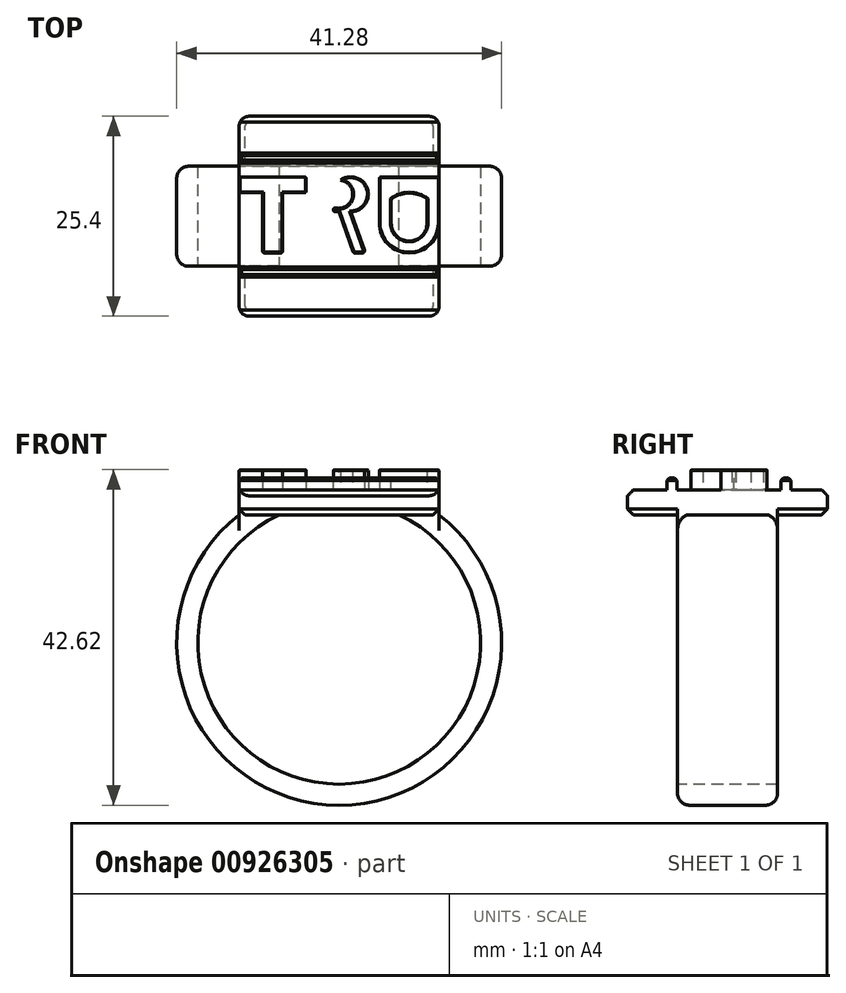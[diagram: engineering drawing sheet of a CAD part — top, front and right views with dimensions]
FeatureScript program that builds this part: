
annotation { "Feature Type Name" : "Feature", "Feature Type Description" : "" }
export const myFeature = defineFeature(function(context is Context, id is Id, definition is map)
    precondition{}
    {
        {
            var Q0;
            Q0=qCreatedBy(makeId("Top.planeOp"),FACE);
            var sketch = newSketch(context, id + "F0", { "sketchPlane" : qUnion([Q0])});
            skLineSegment(sketch, "E0.bottom", {"start": v(12.7, -12.7) * mm, "end": v(-12.7, -12.7) * mm});
            skLineSegment(sketch, "E0.top", {"start": v(12.7, 12.7) * mm, "end": v(-12.7, 12.7) * mm});
            skLineSegment(sketch, "E0.left", {"start": v(12.7, -12.7) * mm, "end": v(12.7, 12.7) * mm});
            skLineSegment(sketch, "E0.right", {"start": v(-12.7, -12.7) * mm, "end": v(-12.7, 12.7) * mm});
            skPoint(sketch, "E0.middle", {"position": v(0, 0) * mm});
            skSolve(sketch);
        }
        {
            var Q0;
            Q0=makeQuery(id+"F0.imprint","IMPRINT",FACE,{"disambiguationData":[TD([[makeQuery(id+"F0.imprint","IMPRINT",EDGE,{"derivedFrom":sQuery(id+"F0.wireOp",EDGE,"E0.bottom")}),-1.0]])]});
            extrude(context, id + "F1", {"entities" : qUnion([Q0]), "depth" : 3.17 * mm, "offsetDistance" : 25.4 * mm});
        }
        {
            var Q0;
            Q0=qCreatedBy(makeId("Front.planeOp"),FACE);
            var sketch = newSketch(context, id + "F2", { "sketchPlane" : qUnion([Q0])});
            skArc(sketch, "E1", {"start": v(-10.16, 0) * mm, "mid": v(0, -35.44) * mm, "end": v(10.16, 0) * mm});
            skSolve(sketch);
        }
        {
            var Q0;
            Q0=makeQuery(id+"F1.opExtrude","CAP_FACE",FACE,{"disambiguationData":[OSD([sQuery(id+"F0.wireOp",EDGE,"E0.bottom"),sQuery(id+"F0.wireOp",EDGE,"E0.top"),sQuery(id+"F0.wireOp",EDGE,"E0.left"),sQuery(id+"F0.wireOp",EDGE,"E0.right")])],"isStart":true});
            var sketch = newSketch(context, id + "F3", { "sketchPlane" : qUnion([Q0])});
            skLineSegment(sketch, "E2.bottom", {"start": v(-7.62, -6.35) * mm, "end": v(-12.7, -6.35) * mm});
            skLineSegment(sketch, "E2.top", {"start": v(-7.62, 6.35) * mm, "end": v(-12.7, 6.35) * mm});
            skLineSegment(sketch, "E2.left", {"start": v(-7.62, -6.35) * mm, "end": v(-7.62, 6.35) * mm});
            skLineSegment(sketch, "E2.right", {"start": v(-12.7, -6.35) * mm, "end": v(-12.7, 6.35) * mm});
            skPoint(sketch, "E2.middle", {"position": v(-10.16, 0) * mm});
            skSolve(sketch);
        }
        {
            var Q0;
            Q0 = qSketchRegion(id + "F3", true);
            var Q1;
            Q1 = qConstructionFilter(qBodyType(qCreatedBy(id + "F3" ,EDGE), BodyType.WIRE), ConstructionObject.NO);
            var Q2;
            Q2 = qConstructionFilter(qBodyType(qCreatedBy(id + "F2" ,EDGE), BodyType.WIRE), ConstructionObject.NO);
            sweep(context, id + "F4", {"operationType" : NewBodyOperationType.ADD, "profiles" : qUnion([Q0]), "surfaceProfiles" : qUnion([Q1]), "path" : qUnion([Q2])});
        }
        {
            var Q0;
            Q0=makeQuery(id+"F1.opExtrude","CAP_FACE",FACE,{"disambiguationData":[OSD([sQuery(id+"F0.wireOp",EDGE,"E0.bottom"),sQuery(id+"F0.wireOp",EDGE,"E0.top"),sQuery(id+"F0.wireOp",EDGE,"E0.left"),sQuery(id+"F0.wireOp",EDGE,"E0.right")])],"isStart":false});
            var sketch = newSketch(context, id + "F5", { "sketchPlane" : qUnion([Q0])});
            skLineSegment(sketch, "E3.bottom", {"start": v(-9.71, 2.99) * mm, "end": v(-7.17, 2.99) * mm});
            skLineSegment(sketch, "E3.top", {"start": v(-9.71, -4.66) * mm, "end": v(-7.17, -4.66) * mm});
            skLineSegment(sketch, "E3.left", {"start": v(-9.71, 2.99) * mm, "end": v(-9.71, -4.66) * mm});
            skLineSegment(sketch, "E3.right", {"start": v(-7.17, 2.99) * mm, "end": v(-7.17, -4.66) * mm});
            skLineSegment(sketch, "E4.bottom", {"start": v(-12.7, 5) * mm, "end": v(-4.19, 5) * mm});
            skLineSegment(sketch, "E4.top", {"start": v(-12.7, 2.99) * mm, "end": v(-4.19, 2.99) * mm});
            skLineSegment(sketch, "E4.left", {"start": v(-12.7, 5) * mm, "end": v(-12.7, 2.99) * mm});
            skLineSegment(sketch, "E4.right", {"start": v(-4.19, 5) * mm, "end": v(-4.19, 2.99) * mm});
            skLineSegment(sketch, "E5", {"start": v(-9.71, -4.66) * mm, "end": v(-12.7, -4.66) * mm});
            skLineSegment(sketch, "E6", {"start": v(-12.7, -4.66) * mm, "end": v(-9.71, -4.66) * mm});
            skLineSegment(sketch, "E7", {"start": v(12.7, -4.66) * mm, "end": v(-7.17, -4.66) * mm});
            skLineSegment(sketch, "E8.bottom", {"start": v(-0.74, 5) * mm, "end": v(-3.28, 5) * mm});
            skLineSegment(sketch, "E8.top", {"start": v(-0.74, -4.66) * mm, "end": v(-3.28, -4.66) * mm});
            skLineSegment(sketch, "E9", {"start": v(-0.74, 5) * mm, "end": v(1.48, 5) * mm});
            skLineSegment(sketch, "E10", {"start": v(5.1, 5) * mm, "end": v(5.1, -0.86) * mm});
            skLineSegment(sketch, "E11", {"start": v(12.7, 5) * mm, "end": v(12.7, -0.86) * mm});
            skLineSegment(sketch, "E12", {"start": v(-12.7, 5) * mm, "end": v(14.85, 5) * mm});
            skLineSegment(sketch, "E13", {"start": v(6.62, 5) * mm, "end": v(6.62, -0.86) * mm});
            skLineSegment(sketch, "E14", {"start": v(11.18, 5) * mm, "end": v(11.18, -0.86) * mm});
            skCircle(sketch, "E15", {"center": v(8.9, -0.86) * mm, "radius": 2.28 * mm});
            skLineSegment(sketch, "E16", {"start": v(6.62, -0.86) * mm, "end": v(5.1, -0.86) * mm});
            skLineSegment(sketch, "E17", {"start": v(11.18, -0.86) * mm, "end": v(12.7, -0.86) * mm});
            skCircle(sketch, "E18", {"center": v(8.9, -0.86) * mm, "radius": 3.8 * mm});
            skLineSegment(sketch, "E19", {"start": v(-3.28, 5) * mm, "end": v(-3.28, -4.66) * mm});
            skLineSegment(sketch, "E20", {"start": v(-0.74, -4.66) * mm, "end": v(-0.74, 5) * mm});
            skLineSegment(sketch, "E21", {"start": v(-0.74, 0.58) * mm, "end": v(1.48, 0.58) * mm});
            skCircle(sketch, "E22", {"center": v(1.48, 2.8) * mm, "radius": 2.22 * mm});
            skLineSegment(sketch, "E23", {"start": v(0, 0.58) * mm, "end": v(1.83, -4.66) * mm});
            skLineSegment(sketch, "E24", {"start": v(1.48, 0.58) * mm, "end": v(3.31, -4.66) * mm});
            skArc(sketch, "E25", {"start": v(-0.74, 1.14) * mm, "mid": v(1.73, 2.8) * mm, "end": v(-0.74, 4.45) * mm});
            skSolve(sketch);
        }
        {
            var Q0;
            {var subQ0=sQuery(id+"F5.wireOp",EDGE,"E4.left");Q0=makeQuery(id+"F5.imprint","IMPRINT",FACE,{"disambiguationData":[TD([[makeQuery(id+"F5.imprint","IMPRINT",EDGE,{"derivedFrom":subQ0}),-1.0]])]});}
            var Q1;
            Q1=makeQuery(id+"F5.imprint","IMPRINT",FACE,{"disambiguationData":[TD([[makeQuery(id+"F5.imprint","IMPRINT",EDGE,{"derivedFrom":sQuery(id+"F5.wireOp",EDGE,"E3.top")}),1.0]])]});
            var Q2;
            {var subQ1=sQuery(id+"F5.wireOp",EDGE,"E8.top");Q2=makeQuery(id+"F5.imprint","IMPRINT",FACE,{"disambiguationData":[TD([[makeQuery(id+"F5.imprint","IMPRINT",EDGE,{"derivedFrom":subQ1}),-1.0]])]});}
            var Q3;
            {var subQ4=sQuery(id+"F5.wireOp",EDGE,"E20");var subQ6=sQuery(id+"F5.wireOp",EDGE,"E12");var subQ7=makeQuery(id+"F5.imprint","INTERSECT",VERTEX,{"derivedFrom":[subQ6,subQ4]});Q3=makeQuery(id+"F5.imprint","IMPRINT",FACE,{"disambiguationData":[TD([[makeQuery(id+"F5.imprint","IMPRINT",EDGE,{"disambiguationData":[TD([[subQ7,-1.0]])],"derivedFrom":subQ6}),-1.0]])]});}
            var Q4;
            Q4=makeQuery(id+"F5.imprint","IMPRINT",FACE,{"disambiguationData":[TD([[makeQuery(id+"F5.imprint","IMPRINT",EDGE,{"derivedFrom":sQuery(id+"F5.wireOp",EDGE,"Z2IO4UIo-EBxe-1SLG-rrHU-Ieeh97X91HPy")}),-1.0]])]});
            var Q5;
            {var subQ0=sQuery(id+"F5.wireOp",EDGE,"E23");Q5=makeQuery(id+"F5.imprint","IMPRINT",FACE,{"disambiguationData":[TD([[makeQuery(id+"F5.imprint","IMPRINT",EDGE,{"derivedFrom":subQ0}),1.0]])]});}
            var Q6;
            {var subQ0=sQuery(id+"F5.wireOp",EDGE,"E10");Q6=makeQuery(id+"F5.imprint","IMPRINT",FACE,{"disambiguationData":[TD([[makeQuery(id+"F5.imprint","IMPRINT",EDGE,{"derivedFrom":subQ0}),1.0]])]});}
            var Q7;
            {var subQ0=sQuery(id+"F5.wireOp",EDGE,"E16");Q7=makeQuery(id+"F5.imprint","IMPRINT",FACE,{"disambiguationData":[TD([[makeQuery(id+"F5.imprint","IMPRINT",EDGE,{"derivedFrom":subQ0}),-1.0]])]});}
            var Q8;
            {var subQ1=sQuery(id+"F5.wireOp",EDGE,"E16");Q8=makeQuery(id+"F5.imprint","IMPRINT",FACE,{"disambiguationData":[TD([[makeQuery(id+"F5.imprint","IMPRINT",EDGE,{"derivedFrom":subQ1}),1.0]])]});}
            var Q9;
            {var subQ1=sQuery(id+"F5.wireOp",EDGE,"E11");Q9=makeQuery(id+"F5.imprint","IMPRINT",FACE,{"disambiguationData":[TD([[makeQuery(id+"F5.imprint","IMPRINT",EDGE,{"derivedFrom":subQ1}),1.0]])]});}
            var Q10;
            {var subQ1=sQuery(id+"F5.wireOp",EDGE,"E14");var subQ3=sQuery(id+"F5.wireOp",EDGE,"E18");var subQ4=makeQuery(id+"F5.imprint","INTERSECT",VERTEX,{"derivedFrom":[subQ1,subQ3]});Q10=makeQuery(id+"F5.imprint","IMPRINT",FACE,{"disambiguationData":[TD([[makeQuery(id+"F5.imprint","IMPRINT",EDGE,{"disambiguationData":[TD([[subQ4,1.0]])],"derivedFrom":subQ3}),1.0]])]});}
            var Q11;
            {var subQ0=sQuery(id+"F5.wireOp",EDGE,"E22");var subQ1=makeQuery(id+"F5.imprint","INTERSECT",VERTEX,{"derivedFrom":[sQuery(id+"F5.wireOp",EDGE,"E12"),subQ0]});Q11=makeQuery(id+"F5.imprint","IMPRINT",FACE,{"disambiguationData":[TD([[makeQuery(id+"F5.imprint","IMPRINT",EDGE,{"disambiguationData":[TD([[subQ1,-1.0]])],"derivedFrom":subQ0}),1.0]])]});}
            var Q12;
            {var subQ1=sQuery(id+"F5.wireOp",EDGE,"E21");var subQ6=sQuery(id+"F5.wireOp",EDGE,"E20");var subQ7=makeQuery(id+"F5.imprint","INTERSECT",VERTEX,{"derivedFrom":[subQ6,subQ1]});Q12=makeQuery(id+"F5.imprint","IMPRINT",FACE,{"disambiguationData":[TD([[makeQuery(id+"F5.imprint","IMPRINT",EDGE,{"disambiguationData":[TD([[subQ7,-1.0]])],"derivedFrom":subQ6}),-1.0]])]});}
            extrude(context, id + "F6", {"entities" : qUnion([Q0, Q1, Q2, Q3, Q4, Q5, Q6, Q7, Q8, Q9, Q10, Q11, Q12]), "operationType" : NewBodyOperationType.ADD, "depth" : 2.54 * mm, "offsetDistance" : 25.4 * mm});
        }
        {
            var Q0;
            Q0=makeQuery(id+"F1.opExtrude","CAP_EDGE",EDGE,{"disambiguationData":[OSD([sQuery(id+"F0.wireOp",EDGE,"E0.bottom")])],"isStart":false});
            var Q1;
            Q1=makeQuery(id+"F1.opExtrude","CAP_EDGE",EDGE,{"disambiguationData":[OSD([sQuery(id+"F0.wireOp",EDGE,"E0.top")])],"isStart":false});
            chamfer(context, id + "F7", {"entities" : qUnion([Q0, Q1]), "width" : 0.76 * mm, "tangentPropagation" : true});
        }
        {
            var Q0;
            Q0=makeQuery(id+"F1.opExtrude","SWEPT_EDGE",EDGE,{"disambiguationData":[OSD([sQuery(id+"F0.wireOp",EDGE,"E0.bottom"),sQuery(id+"F0.wireOp",EDGE,"E0.left")])]});
            var Q1;
            Q1=makeQuery(id+"F1.opExtrude","SWEPT_EDGE",EDGE,{"disambiguationData":[OSD([sQuery(id+"F0.wireOp",EDGE,"E0.bottom"),sQuery(id+"F0.wireOp",EDGE,"E0.right")])]});
            var Q2;
            Q2=makeQuery(id+"F1.opExtrude","SWEPT_EDGE",EDGE,{"disambiguationData":[OSD([sQuery(id+"F0.wireOp",EDGE,"E0.top"),sQuery(id+"F0.wireOp",EDGE,"E0.left")])]});
            var Q3;
            Q3=makeQuery(id+"F1.opExtrude","SWEPT_EDGE",EDGE,{"disambiguationData":[OSD([sQuery(id+"F0.wireOp",EDGE,"E0.top"),sQuery(id+"F0.wireOp",EDGE,"E0.right")])]});
            fillet(context, id + "F8", {"entities" : qUnion([Q0, Q1, Q2, Q3]), "radius" : 1.27 * mm, "tangentPropagation" : true, "allowEdgeOverflow" : false});
        }
        {
            var Q0;
            Q0=makeQuery(id+"F1.opExtrude","CAP_EDGE",EDGE,{"disambiguationData":[OSD([sQuery(id+"F0.wireOp",EDGE,"E0.bottom")])],"isStart":true});
            var Q1;
            {var subQ1=sQuery(id+"F0.wireOp",EDGE,"E0.right");var subQ2=sQuery(id+"F0.wireOp",EDGE,"E0.bottom");Q1=makeQuery(id+"F4.boolean.opBoolean","SPLIT",EDGE,{"disambiguationData":[TD([makeQuery(id+"F1.opExtrude","SWEPT_FACE",FACE,{"disambiguationData":[OSD([subQ2])]})])],"derivedFrom":makeQuery(id+"F1.opExtrude","CAP_EDGE",EDGE,{"disambiguationData":[OSD([subQ1])],"isStart":true})});}
            var Q2;
            {var subQ1=sQuery(id+"F0.wireOp",EDGE,"E0.left");var subQ2=makeQuery(id+"F1.opExtrude","SWEPT_FACE",FACE,{"disambiguationData":[OSD([subQ1])]});var subQ3=sQuery(id+"F0.wireOp",EDGE,"E0.bottom");var subQ4=makeQuery(id+"F1.opExtrude","CAP_FACE",FACE,{"disambiguationData":[OSD([subQ3,sQuery(id+"F0.wireOp",EDGE,"E0.top"),subQ1,sQuery(id+"F0.wireOp",EDGE,"E0.right")])],"isStart":true});Q2=makeQuery(id+"F4.boolean.opBoolean","SPLIT",EDGE,{"disambiguationData":[topologyDisambiguationEdgeConnected([subQ4,subQ2]),TD([makeQuery(id+"F1.opExtrude","SWEPT_FACE",FACE,{"disambiguationData":[OSD([subQ3])]})])],"derivedFrom":makeQuery(id+"F1.opExtrude","CAP_EDGE",EDGE,{"disambiguationData":[OSD([subQ1])],"isStart":true})});}
            var Q3;
            {var subQ0=sQuery(id+"F0.wireOp",EDGE,"E0.left");var subQ1=makeQuery(id+"F1.opExtrude","SWEPT_FACE",FACE,{"disambiguationData":[OSD([subQ0])]});var subQ3=sQuery(id+"F0.wireOp",EDGE,"E0.top");var subQ4=makeQuery(id+"F1.opExtrude","CAP_FACE",FACE,{"disambiguationData":[OSD([sQuery(id+"F0.wireOp",EDGE,"E0.bottom"),subQ3,subQ0,sQuery(id+"F0.wireOp",EDGE,"E0.right")])],"isStart":true});Q3=makeQuery(id+"F4.boolean.opBoolean","SPLIT",EDGE,{"disambiguationData":[topologyDisambiguationEdgeConnected([subQ4,subQ1]),TD([makeQuery(id+"F1.opExtrude","SWEPT_FACE",FACE,{"disambiguationData":[OSD([subQ3])]})])],"derivedFrom":makeQuery(id+"F1.opExtrude","CAP_EDGE",EDGE,{"disambiguationData":[OSD([subQ0])],"isStart":true})});}
            var Q4;
            {var subQ0=sQuery(id+"F0.wireOp",EDGE,"E0.right");var subQ2=sQuery(id+"F0.wireOp",EDGE,"E0.top");Q4=makeQuery(id+"F4.boolean.opBoolean","SPLIT",EDGE,{"disambiguationData":[TD([makeQuery(id+"F1.opExtrude","SWEPT_FACE",FACE,{"disambiguationData":[OSD([subQ2])]})])],"derivedFrom":makeQuery(id+"F1.opExtrude","CAP_EDGE",EDGE,{"disambiguationData":[OSD([subQ0])],"isStart":true})});}
            var Q5;
            Q5=makeQuery(id+"F1.opExtrude","CAP_EDGE",EDGE,{"disambiguationData":[OSD([sQuery(id+"F0.wireOp",EDGE,"E0.top")])],"isStart":true});
            chamfer(context, id + "F9", {"entities" : qUnion([Q0, Q1, Q2, Q3, Q4, Q5]), "width" : 0.76 * mm, "tangentPropagation" : true});
        }
        {
            var Q0;
            Q0=makeQuery(id+"F6.opExtrude","CAP_EDGE",EDGE,{"disambiguationData":[OSD([sQuery(id+"F5.wireOp",EDGE,"E3.left")])],"isStart":false});
            var Q1;
            Q1=makeQuery(id+"F6.opExtrude","CAP_EDGE",EDGE,{"disambiguationData":[OSD([sQuery(id+"F5.wireOp",EDGE,"E3.top")])],"isStart":false});
            var Q2;
            Q2=makeQuery(id+"F6.opExtrude","CAP_EDGE",EDGE,{"disambiguationData":[OSD([sQuery(id+"F5.wireOp",EDGE,"E3.right")])],"isStart":false});
            var Q3;
            {var subQ0=sQuery(id+"F5.wireOp",EDGE,"E4.top");Q3=makeQuery(id+"F6.opExtrude","CAP_EDGE",EDGE,{"disambiguationData":[OSD([subQ0]),TDD([makeQuery(id+"F5.imprint","IMPRINT",EDGE,{"disambiguationData":[TD([[makeQuery(id+"F5.imprint","INTERSECT",VERTEX,{"derivedFrom":[sQuery(id+"F5.wireOp",EDGE,"E3.right"),subQ0]}),-1.0]])],"derivedFrom":subQ0})])],"isStart":false});}
            var Q4;
            Q4=makeQuery(id+"F6.opExtrude","CAP_EDGE",EDGE,{"disambiguationData":[OSD([sQuery(id+"F5.wireOp",EDGE,"E4.right")])],"isStart":false});
            var Q5;
            {var subQ0=sQuery(id+"F5.wireOp",EDGE,"E12");Q5=makeQuery(id+"F6.opExtrude","CAP_EDGE",EDGE,{"disambiguationData":[OSD([subQ0]),TDD([makeQuery(id+"F5.imprint","IMPRINT",EDGE,{"disambiguationData":[TD([[makeQuery(id+"F5.imprint","INTERSECT",VERTEX,{"derivedFrom":[sQuery(id+"F5.wireOp",EDGE,"E4.right"),subQ0]}),1.0]])],"derivedFrom":subQ0})])],"isStart":false});}
            var Q6;
            Q6=makeQuery(id+"F6.opExtrude","CAP_EDGE",EDGE,{"disambiguationData":[OSD([sQuery(id+"F5.wireOp",EDGE,"E4.left")])],"isStart":false});
            var Q7;
            {var subQ0=sQuery(id+"F5.wireOp",EDGE,"E4.top");Q7=makeQuery(id+"F6.opExtrude","CAP_EDGE",EDGE,{"disambiguationData":[OSD([subQ0]),TDD([makeQuery(id+"F5.imprint","IMPRINT",EDGE,{"disambiguationData":[TD([[makeQuery(id+"F5.imprint","INTERSECT",VERTEX,{"derivedFrom":[sQuery(id+"F5.wireOp",EDGE,"E3.left"),subQ0]}),1.0]])],"derivedFrom":subQ0})])],"isStart":false});}
            var Q8;
            Q8=makeQuery(id+"F6.opExtrude","CAP_EDGE",EDGE,{"disambiguationData":[OSD([sQuery(id+"F5.wireOp",EDGE,"E19")])],"isStart":false});
            var Q9;
            Q9=makeQuery(id+"F6.opExtrude","CAP_EDGE",EDGE,{"disambiguationData":[OSD([sQuery(id+"F5.wireOp",EDGE,"E8.top")])],"isStart":false});
            var Q10;
            {var subQ0=sQuery(id+"F5.wireOp",EDGE,"E20");Q10=makeQuery(id+"F6.opExtrude","CAP_EDGE",EDGE,{"disambiguationData":[OSD([subQ0]),TDD([makeQuery(id+"F5.imprint","IMPRINT",EDGE,{"disambiguationData":[TD([[makeQuery(id+"F5.imprint","INTERSECT",VERTEX,{"derivedFrom":[subQ0,sQuery(id+"F5.wireOp",EDGE,"E21")]}),1.0]])],"derivedFrom":subQ0})])],"isStart":false});}
            var Q11;
            {var subQ0=sQuery(id+"F5.wireOp",EDGE,"E25");var subQ1=sQuery(id+"F5.wireOp",EDGE,"E20");Q11=makeQuery(id+"F6.opExtrude","CAP_EDGE",EDGE,{"disambiguationData":[OSD([subQ1]),TDD([makeQuery(id+"F5.imprint","IMPRINT",EDGE,{"disambiguationData":[TD([[makeQuery(id+"F5.imprint","INTERSECT",VERTEX,{"disambiguationData":[OD(0.0)],"derivedFrom":[subQ1,subQ0]}),-1.0]])],"derivedFrom":subQ1})])],"isStart":false});}
            var Q12;
            Q12=makeQuery(id+"F6.opExtrude","CAP_EDGE",EDGE,{"disambiguationData":[OSD([sQuery(id+"F5.wireOp",EDGE,"E25")])],"isStart":false});
            var Q13;
            {var subQ0=sQuery(id+"F5.wireOp",EDGE,"E12");var subQ1=makeQuery(id+"F5.imprint","INTERSECT",VERTEX,{"derivedFrom":[subQ0,sQuery(id+"F5.wireOp",EDGE,"E20")]});Q13=makeQuery(id+"F6.opExtrude","CAP_EDGE",EDGE,{"disambiguationData":[OSD([subQ0]),TDD([makeQuery(id+"F5.imprint","IMPRINT",EDGE,{"disambiguationData":[TD([[makeQuery(id+"F5.imprint","INTERSECT",VERTEX,{"derivedFrom":[subQ0,sQuery(id+"F5.wireOp",EDGE,"E19")]}),-1.0]])],"derivedFrom":subQ0}),makeQuery(id+"F5.imprint","IMPRINT",EDGE,{"disambiguationData":[TD([[subQ1,-1.0]])],"derivedFrom":subQ0})])],"isStart":false});}
            var Q14;
            Q14=makeQuery(id+"F6.opExtrude","CAP_EDGE",EDGE,{"disambiguationData":[OSD([sQuery(id+"F5.wireOp",EDGE,"E22")])],"isStart":false});
            var Q15;
            Q15=makeQuery(id+"F6.opExtrude","CAP_EDGE",EDGE,{"disambiguationData":[OSD([sQuery(id+"F5.wireOp",EDGE,"E24")])],"isStart":false});
            var Q16;
            Q16=makeQuery(id+"F6.opExtrude","CAP_EDGE",EDGE,{"disambiguationData":[OSD([sQuery(id+"F5.wireOp",EDGE,"E23")])],"isStart":false});
            var Q17;
            Q17=makeQuery(id+"F6.opExtrude","CAP_EDGE",EDGE,{"disambiguationData":[OSD([sQuery(id+"F5.wireOp",EDGE,"E7")])],"isStart":false});
            var Q18;
            Q18=makeQuery(id+"F6.opExtrude","CAP_EDGE",EDGE,{"disambiguationData":[OSD([sQuery(id+"F5.wireOp",EDGE,"E21")])],"isStart":false});
            var Q19;
            Q19=makeQuery(id+"F6.opExtrude","CAP_EDGE",EDGE,{"disambiguationData":[OSD([sQuery(id+"F5.wireOp",EDGE,"E10")])],"isStart":false});
            var Q20;
            Q20=makeQuery(id+"F6.opExtrude","CAP_EDGE",EDGE,{"disambiguationData":[OSD([sQuery(id+"F5.wireOp",EDGE,"E13")])],"isStart":false});
            var Q21;
            {var subQ0=sQuery(id+"F5.wireOp",EDGE,"E12");Q21=makeQuery(id+"F6.opExtrude","CAP_EDGE",EDGE,{"disambiguationData":[OSD([subQ0]),TDD([makeQuery(id+"F5.imprint","IMPRINT",EDGE,{"disambiguationData":[TD([[makeQuery(id+"F5.imprint","INTERSECT",VERTEX,{"derivedFrom":[sQuery(id+"F5.wireOp",EDGE,"E10"),subQ0]}),-1.0]])],"derivedFrom":subQ0})])],"isStart":false});}
            var Q22;
            Q22=makeQuery(id+"F6.opExtrude","CAP_EDGE",EDGE,{"disambiguationData":[OSD([sQuery(id+"F5.wireOp",EDGE,"E18")])],"isStart":false});
            var Q23;
            Q23=makeQuery(id+"F6.opExtrude","CAP_EDGE",EDGE,{"disambiguationData":[OSD([sQuery(id+"F5.wireOp",EDGE,"E14")])],"isStart":false});
            var Q24;
            {var subQ0=sQuery(id+"F5.wireOp",EDGE,"E12");Q24=makeQuery(id+"F6.opExtrude","CAP_EDGE",EDGE,{"disambiguationData":[OSD([subQ0]),TDD([makeQuery(id+"F5.imprint","IMPRINT",EDGE,{"disambiguationData":[TD([[makeQuery(id+"F5.imprint","INTERSECT",VERTEX,{"derivedFrom":[subQ0,sQuery(id+"F5.wireOp",EDGE,"E14")]}),-1.0]])],"derivedFrom":subQ0})])],"isStart":false});}
            var Q25;
            Q25=makeQuery(id+"F6.opExtrude","CAP_EDGE",EDGE,{"disambiguationData":[OSD([sQuery(id+"F5.wireOp",EDGE,"E15")])],"isStart":false});
            chamfer(context, id + "F10", {"entities" : qUnion([Q0, Q1, Q2, Q3, Q4, Q5, Q6, Q7, Q8, Q9, Q10, Q11, Q12, Q13, Q14, Q15, Q16, Q17, Q18, Q19, Q20, Q21, Q22, Q23, Q24, Q25]), "width" : 0.1 * mm, "tangentPropagation" : true});
        }
        {
            var Q0;
            Q0=makeQuery(id+"F6.opExtrude","CAP_EDGE",EDGE,{"disambiguationData":[OSD([sQuery(id+"F5.wireOp",EDGE,"E11")])],"isStart":false});
            chamfer(context, id + "F11", {"entities" : qUnion([Q0]), "width" : 0.1 * mm, "tangentPropagation" : true});
        }
        {
            var Q0;
            Q0=makeQuery(id+"F6.opExtrude","SWEPT_EDGE",EDGE,{"disambiguationData":[OSD([sQuery(id+"F5.wireOp",EDGE,"E3.top"),sQuery(id+"F5.wireOp",EDGE,"E3.right"),sQuery(id+"F5.wireOp",EDGE,"E7")])]});
            var Q1;
            Q1=makeQuery(id+"F6.opExtrude","SWEPT_EDGE",EDGE,{"disambiguationData":[OSD([sQuery(id+"F5.wireOp",EDGE,"E3.top"),sQuery(id+"F5.wireOp",EDGE,"E3.left"),sQuery(id+"F5.wireOp",EDGE,"E6")])]});
            fillet(context, id + "F12", {"entities" : qUnion([Q0, Q1]), "radius" : 0.25 * mm, "tangentPropagation" : true, "allowEdgeOverflow" : false});
        }
        {
            var Q0;
            Q0=makeQuery(id+"F6.opExtrude","SWEPT_EDGE",EDGE,{"disambiguationData":[OSD([sQuery(id+"F5.wireOp",EDGE,"E3.left"),sQuery(id+"F5.wireOp",EDGE,"E4.top")])]});
            var Q1;
            Q1=makeQuery(id+"F6.opExtrude","SWEPT_EDGE",EDGE,{"disambiguationData":[OSD([sQuery(id+"F0.wireOp",EDGE,"E0.right"),sQuery(id+"F5.wireOp",EDGE,"E4.top"),sQuery(id+"F5.wireOp",EDGE,"E4.left")])]});
            var Q2;
            Q2=makeQuery(id+"F6.opExtrude","SWEPT_EDGE",EDGE,{"disambiguationData":[OSD([sQuery(id+"F0.wireOp",EDGE,"E0.right"),sQuery(id+"F5.wireOp",EDGE,"E4.left"),sQuery(id+"F5.wireOp",EDGE,"E12")])]});
            var Q3;
            Q3=makeQuery(id+"F6.opExtrude","SWEPT_EDGE",EDGE,{"disambiguationData":[OSD([sQuery(id+"F5.wireOp",EDGE,"E3.right"),sQuery(id+"F5.wireOp",EDGE,"E4.top")])]});
            var Q4;
            Q4=makeQuery(id+"F6.opExtrude","SWEPT_EDGE",EDGE,{"disambiguationData":[OSD([sQuery(id+"F5.wireOp",EDGE,"E4.top"),sQuery(id+"F5.wireOp",EDGE,"E4.right")])]});
            var Q5;
            Q5=makeQuery(id+"F6.opExtrude","SWEPT_EDGE",EDGE,{"disambiguationData":[OSD([sQuery(id+"F5.wireOp",EDGE,"E4.right"),sQuery(id+"F5.wireOp",EDGE,"E12")])]});
            fillet(context, id + "F13", {"entities" : qUnion([Q0, Q1, Q2, Q3, Q4, Q5]), "radius" : 0.25 * mm, "tangentPropagation" : true, "allowEdgeOverflow" : false});
        }
        {
            var Q0;
            Q0=makeQuery(id+"F6.opExtrude","SWEPT_EDGE",EDGE,{"disambiguationData":[OSD([sQuery(id+"F5.wireOp",EDGE,"E7"),sQuery(id+"F5.wireOp",EDGE,"E8.top"),sQuery(id+"F5.wireOp",EDGE,"E19")])]});
            var Q1;
            Q1=makeQuery(id+"F6.opExtrude","SWEPT_EDGE",EDGE,{"disambiguationData":[OSD([sQuery(id+"F5.wireOp",EDGE,"E7"),sQuery(id+"F5.wireOp",EDGE,"E8.top"),sQuery(id+"F5.wireOp",EDGE,"E20")])]});
            var Q2;
            Q2=makeQuery(id+"F6.opExtrude","SWEPT_EDGE",EDGE,{"disambiguationData":[OSD([sQuery(id+"F5.wireOp",EDGE,"E7"),sQuery(id+"F5.wireOp",EDGE,"E23")])]});
            var Q3;
            Q3=makeQuery(id+"F6.opExtrude","SWEPT_EDGE",EDGE,{"disambiguationData":[OSD([sQuery(id+"F5.wireOp",EDGE,"E7"),sQuery(id+"F5.wireOp",EDGE,"E24")])]});
            var Q4;
            Q4=makeQuery(id+"F6.opExtrude","SWEPT_EDGE",EDGE,{"disambiguationData":[OSD([sQuery(id+"F5.wireOp",EDGE,"E21"),sQuery(id+"F5.wireOp",EDGE,"E23")])]});
            var Q5;
            Q5=makeQuery(id+"F6.opExtrude","SWEPT_EDGE",EDGE,{"disambiguationData":[OSD([sQuery(id+"F5.wireOp",EDGE,"E20"),sQuery(id+"F5.wireOp",EDGE,"E21")])]});
            var Q6;
            Q6=makeQuery(id+"F6.opExtrude","SWEPT_EDGE",EDGE,{"disambiguationData":[OSD([sQuery(id+"F5.wireOp",EDGE,"E21"),sQuery(id+"F5.wireOp",EDGE,"E22"),sQuery(id+"F5.wireOp",EDGE,"E24")])]});
            var Q7;
            Q7=makeQuery(id+"F6.opExtrude","SWEPT_EDGE",EDGE,{"disambiguationData":[OSD([sQuery(id+"F5.wireOp",EDGE,"E12"),sQuery(id+"F5.wireOp",EDGE,"E19")])]});
            fillet(context, id + "F14", {"entities" : qUnion([Q0, Q1, Q2, Q3, Q4, Q5, Q6, Q7]), "radius" : 0.25 * mm, "tangentPropagation" : true, "allowEdgeOverflow" : false});
        }
        {
            var Q0;
            Q0=makeQuery(id+"F6.opExtrude","SWEPT_EDGE",EDGE,{"disambiguationData":[OSD([sQuery(id+"F5.wireOp",EDGE,"E10"),sQuery(id+"F5.wireOp",EDGE,"E12")])]});
            var Q1;
            Q1=makeQuery(id+"F6.opExtrude","SWEPT_EDGE",EDGE,{"disambiguationData":[OSD([sQuery(id+"F5.wireOp",EDGE,"E12"),sQuery(id+"F5.wireOp",EDGE,"E13")])]});
            var Q2;
            Q2=makeQuery(id+"F6.opExtrude","SWEPT_EDGE",EDGE,{"disambiguationData":[OSD([sQuery(id+"F5.wireOp",EDGE,"E12"),sQuery(id+"F5.wireOp",EDGE,"E14")])]});
            var Q3;
            Q3=makeQuery(id+"F6.opExtrude","SWEPT_EDGE",EDGE,{"disambiguationData":[OSD([sQuery(id+"F0.wireOp",EDGE,"E0.left"),sQuery(id+"F5.wireOp",EDGE,"E11"),sQuery(id+"F5.wireOp",EDGE,"E12")])]});
            fillet(context, id + "F15", {"entities" : qUnion([Q0, Q1, Q2, Q3]), "radius" : 0.25 * mm, "tangentPropagation" : true, "allowEdgeOverflow" : false});
        }
        {
            var Q0;
            {var subQ4=sQuery(id+"F0.wireOp",EDGE,"E0.left");var subQ11=sQuery(id+"F0.wireOp",EDGE,"E0.right");var subQ16=sQuery(id+"F0.wireOp",EDGE,"E0.bottom");var subQ19=sQuery(id+"F0.wireOp",EDGE,"E0.top");Q0=makeQuery(id+"F6.boolean.opBoolean","SPLIT",FACE,{"disambiguationData":[TD([makeQuery(id+"F1.opExtrude","SWEPT_FACE",FACE,{"disambiguationData":[OSD([subQ16])]})])],"derivedFrom":makeQuery(id+"F1.opExtrude","CAP_FACE",FACE,{"disambiguationData":[OSD([subQ16,subQ19,subQ4,subQ11])],"isStart":false})});}
            var sketch = newSketch(context, id + "F16", { "sketchPlane" : qUnion([Q0])});
            skLineSegment(sketch, "E26.bottom", {"start": v(-12.7, -6.44) * mm, "end": v(12.7, -6.44) * mm});
            skLineSegment(sketch, "E26.top", {"start": v(-12.7, -7.7) * mm, "end": v(12.7, -7.7) * mm});
            skLineSegment(sketch, "E26.left", {"start": v(-12.7, -6.44) * mm, "end": v(-12.7, -7.7) * mm});
            skLineSegment(sketch, "E26.right", {"start": v(12.7, -6.44) * mm, "end": v(12.7, -7.7) * mm});
            skLineSegment(sketch, "E27.bottom", {"start": v(-12.7, 8.06) * mm, "end": v(12.7, 8.06) * mm});
            skLineSegment(sketch, "E27.top", {"start": v(-12.7, 6.79) * mm, "end": v(12.7, 6.79) * mm});
            skLineSegment(sketch, "E27.left", {"start": v(-12.7, 8.06) * mm, "end": v(-12.7, 6.79) * mm});
            skLineSegment(sketch, "E27.right", {"start": v(12.7, 8.06) * mm, "end": v(12.7, 6.79) * mm});
            skSolve(sketch);
        }
        {
            var Q0;
            Q0=makeQuery(id+"F16.imprint","IMPRINT",FACE,{"disambiguationData":[TD([[makeQuery(id+"F16.imprint","IMPRINT",EDGE,{"derivedFrom":sQuery(id+"F16.wireOp",EDGE,"E27.bottom")}),-1.0]])]});
            var Q1;
            Q1=makeQuery(id+"F16.imprint","IMPRINT",FACE,{"disambiguationData":[TD([[makeQuery(id+"F16.imprint","IMPRINT",EDGE,{"derivedFrom":sQuery(id+"F16.wireOp",EDGE,"E26.bottom")}),-1.0]])]});
            extrude(context, id + "F17", {"entities" : qUnion([Q0, Q1]), "operationType" : NewBodyOperationType.ADD, "depth" : 1.52 * mm, "offsetDistance" : 25.4 * mm});
        }
        {
            var Q0;
            Q0=makeQuery(id+"F17.opExtrude","CAP_EDGE",EDGE,{"disambiguationData":[OSD([sQuery(id+"F16.wireOp",EDGE,"E26.left")])],"isStart":false});
            var Q1;
            Q1=makeQuery(id+"F17.opExtrude","CAP_EDGE",EDGE,{"disambiguationData":[OSD([sQuery(id+"F16.wireOp",EDGE,"E26.bottom")])],"isStart":false});
            var Q2;
            Q2=makeQuery(id+"F17.opExtrude","CAP_EDGE",EDGE,{"disambiguationData":[OSD([sQuery(id+"F16.wireOp",EDGE,"E26.right")])],"isStart":false});
            var Q3;
            Q3=makeQuery(id+"F17.opExtrude","CAP_EDGE",EDGE,{"disambiguationData":[OSD([sQuery(id+"F16.wireOp",EDGE,"E26.top")])],"isStart":false});
            var Q4;
            Q4=makeQuery(id+"F17.opExtrude","CAP_EDGE",EDGE,{"disambiguationData":[OSD([sQuery(id+"F16.wireOp",EDGE,"E27.bottom")])],"isStart":false});
            var Q5;
            Q5=makeQuery(id+"F17.opExtrude","CAP_EDGE",EDGE,{"disambiguationData":[OSD([sQuery(id+"F16.wireOp",EDGE,"E27.top")])],"isStart":false});
            var Q6;
            Q6=makeQuery(id+"F17.opExtrude","CAP_EDGE",EDGE,{"disambiguationData":[OSD([sQuery(id+"F16.wireOp",EDGE,"E27.left")])],"isStart":false});
            var Q7;
            Q7=makeQuery(id+"F17.opExtrude","CAP_EDGE",EDGE,{"disambiguationData":[OSD([sQuery(id+"F16.wireOp",EDGE,"E27.right")])],"isStart":false});
            chamfer(context, id + "F18", {"entities" : qUnion([Q0, Q1, Q2, Q3, Q4, Q5, Q6, Q7]), "width" : 0.33 * mm, "tangentPropagation" : true});
        }
        {
            var Q0;
            Q0=qCreatedBy(makeId("Front.planeOp"),FACE);
            var sketch = newSketch(context, id + "F19", { "sketchPlane" : qUnion([Q0])});
            skLineSegment(sketch, "E28.0", {"start": v(11.43, 0) * mm, "end": v(-11.43, 0) * mm});
            skArc(sketch, "E28.1", {"start": v(-7.62, 0) * mm, "mid": v(0, -34.23) * mm, "end": v(7.62, 0) * mm});
            skLineSegment(sketch, "E28.2", {"start": v(11.27, -2.28) * mm, "end": v(10.16, 0) * mm});
            skSolve(sketch);
        }
        {
            var Q0;
            {var subQ3=sQuery(id+"F19.wireOp",EDGE,"E28.2");Q0=makeQuery(id+"F19.imprint","IMPRINT",FACE,{"disambiguationData":[TD([[makeQuery(id+"F19.imprint","IMPRINT",EDGE,{"derivedFrom":subQ3}),1.0]])]});}
            var Q1;
            Q1=makeQuery(id+"F4.opSweep","SWEPT_FACE",FACE,{"disambiguationData":[OSD([sQuery(id+"F2.wireOp",EDGE,"E1"),sQuery(id+"F3.wireOp",EDGE,"E2.top")])]});
            var Q2;
            Q2=makeQuery(id+"F4.opSweep","SWEPT_FACE",FACE,{"disambiguationData":[OSD([sQuery(id+"F2.wireOp",EDGE,"E1"),sQuery(id+"F3.wireOp",EDGE,"E2.bottom")])]});
            extrude(context, id + "F20", {"entities" : qUnion([Q0]), "operationType" : NewBodyOperationType.ADD, "endBound" : BoundingType.UP_TO_SURFACE, "depth" : 25.4 * mm, "endBoundEntityFace" : qUnion([Q1]), "offsetDistance" : 25.4 * mm, "hasSecondDirection" : true, "secondDirectionBound" : SecondDirectionBoundingType.UP_TO_SURFACE, "secondDirectionOppositeDirection" : true, "secondDirectionDepth" : 25.4 * mm, "secondDirectionBoundEntityFace" : qUnion([Q2])});
        }
        {
            var Q0;
            Q0=makeQuery(id+"F4.opSweep","SWEPT_EDGE",EDGE,{"disambiguationData":[OSD([sQuery(id+"F0.wireOp",EDGE,"E0.right"),sQuery(id+"F2.wireOp",EDGE,"E1"),sQuery(id+"F3.wireOp",EDGE,"E2.top"),sQuery(id+"F3.wireOp",EDGE,"E2.right")])]});
            var Q1;
            Q1=makeQuery(id+"F4.opSweep","SWEPT_EDGE",EDGE,{"disambiguationData":[OSD([sQuery(id+"F0.wireOp",EDGE,"E0.right"),sQuery(id+"F2.wireOp",EDGE,"E1"),sQuery(id+"F3.wireOp",EDGE,"E2.bottom"),sQuery(id+"F3.wireOp",EDGE,"E2.right")])]});
            fillet(context, id + "F21", {"entities" : qUnion([Q0, Q1]), "radius" : 1.52 * mm, "tangentPropagation" : true, "allowEdgeOverflow" : false});
        }
    });
